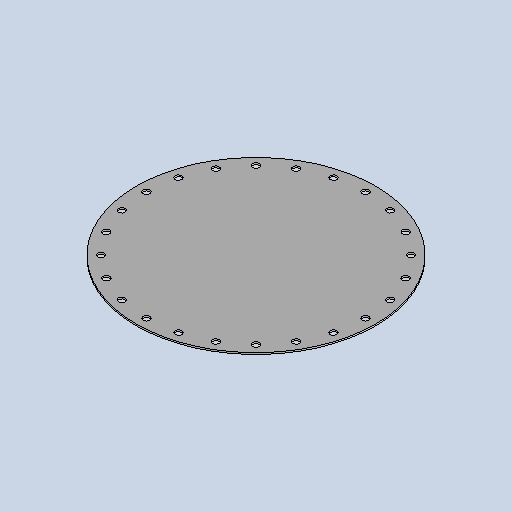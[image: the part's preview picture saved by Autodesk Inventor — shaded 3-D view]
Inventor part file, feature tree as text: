
AUTODESK INVENTOR PART (.ipt)
format: ipt  version: 2025 (Build 290162010, 162A)  size: 157,696 bytes
history: native  units: mm
features: sketch x2, other x2, sheet_metal_op x1, extrude x1, pattern_circular x1
ambient origin geometry x8: Origin, YZ Plane, XZ Plane, XY Plane, X Axis, Y Axis, Z Axis, Center Point
bodies: Solid1 (feature_tree)
feature tree (7):
  sheet_metal_op  "Face1"
  extrude  "Extrusion1"  Depth=4.0mm
  pattern_circular  "Circular Pattern1"  Count=55  [1 undecoded]
  sketch  "Sketch1"  dims[d0=600.0mm d1=4.0mm d2=550.0mm]
  other  "Plate1"
  sketch  "Sketch2"  dims[d3=17.0mm d4=0.0mm d5=0.0mm d6=240.0mm d7=360.0deg]
  other  "Definition1"
note: 1 required parameter value undecoded (feature->parameter linkage not recoverable at this tier; creation-order binding heuristic only, values carry confidence <= 0.55)
